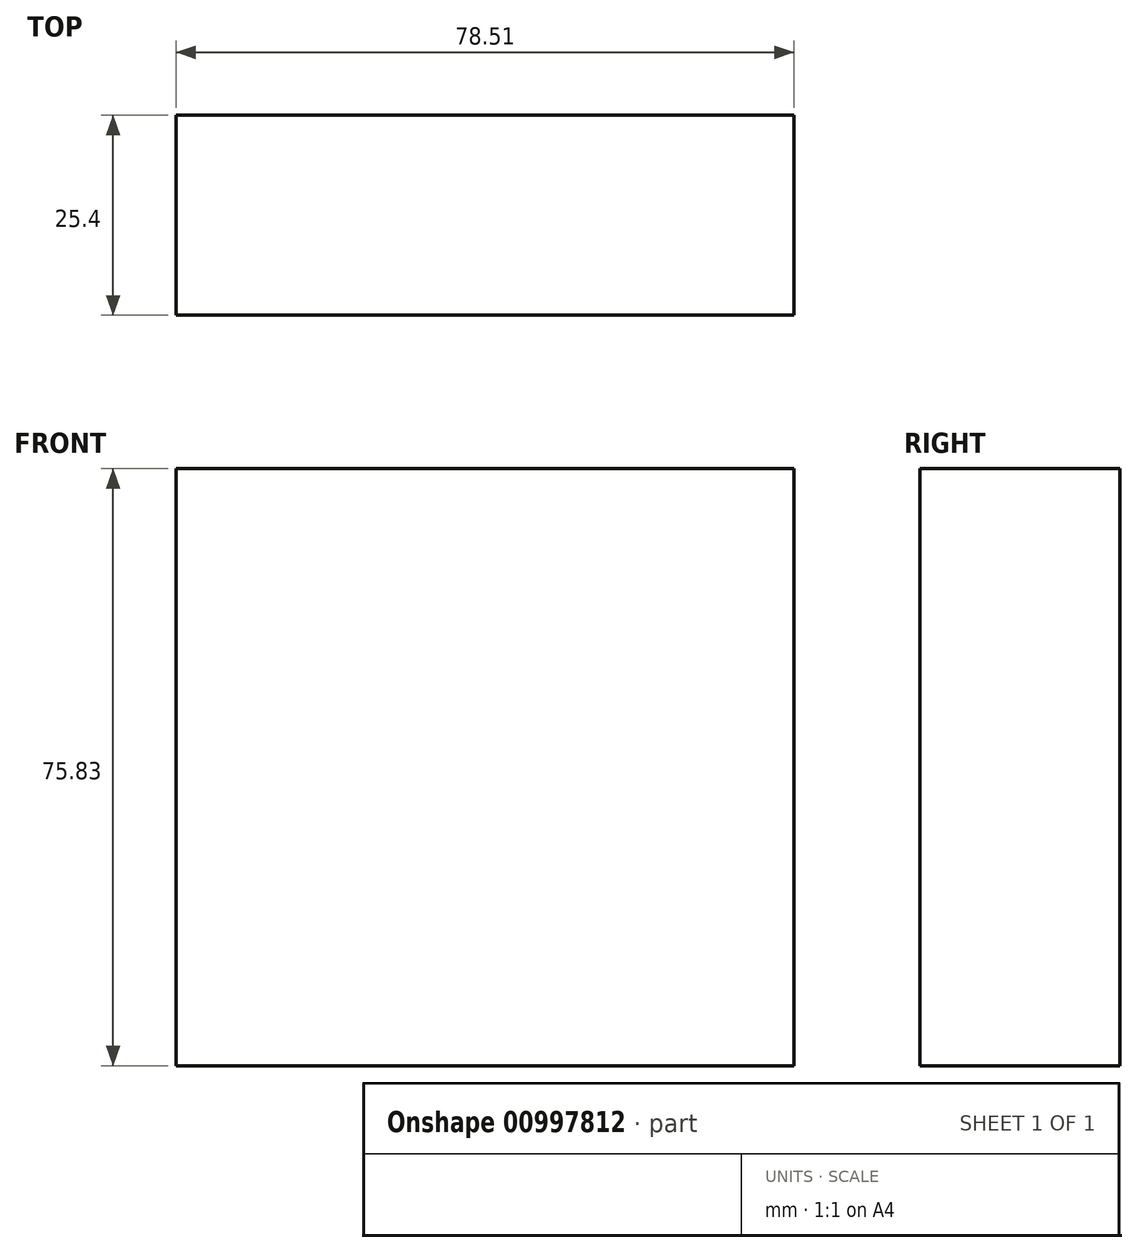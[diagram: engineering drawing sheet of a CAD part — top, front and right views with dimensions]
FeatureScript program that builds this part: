
annotation { "Feature Type Name" : "Feature", "Feature Type Description" : "" }
export const myFeature = defineFeature(function(context is Context, id is Id, definition is map)
    precondition{}
    {
        {
            var Q0;
            Q0=qCreatedBy(makeId("Front.planeOp"),FACE);
            var sketch = newSketch(context, id + "F0", { "sketchPlane" : qUnion([Q0])});
            skLineSegment(sketch, "E0.bottom", {"start": v(-83.72, 39.71) * mm, "end": v(-5.21, 39.71) * mm});
            skLineSegment(sketch, "E0.top", {"start": v(-83.72, -36.12) * mm, "end": v(-5.21, -36.12) * mm});
            skLineSegment(sketch, "E0.left", {"start": v(-83.72, 39.71) * mm, "end": v(-83.72, -36.12) * mm});
            skLineSegment(sketch, "E0.right", {"start": v(-5.21, 39.71) * mm, "end": v(-5.21, -36.12) * mm});
            skSolve(sketch);
        }
        {
            var Q0;
            Q0 = qSketchRegion(id + "F0", true);
            extrude(context, id + "F1", {"entities" : qUnion([Q0]), "depth" : 25.4 * mm, "offsetDistance" : 25.4 * mm});
        }
    });
